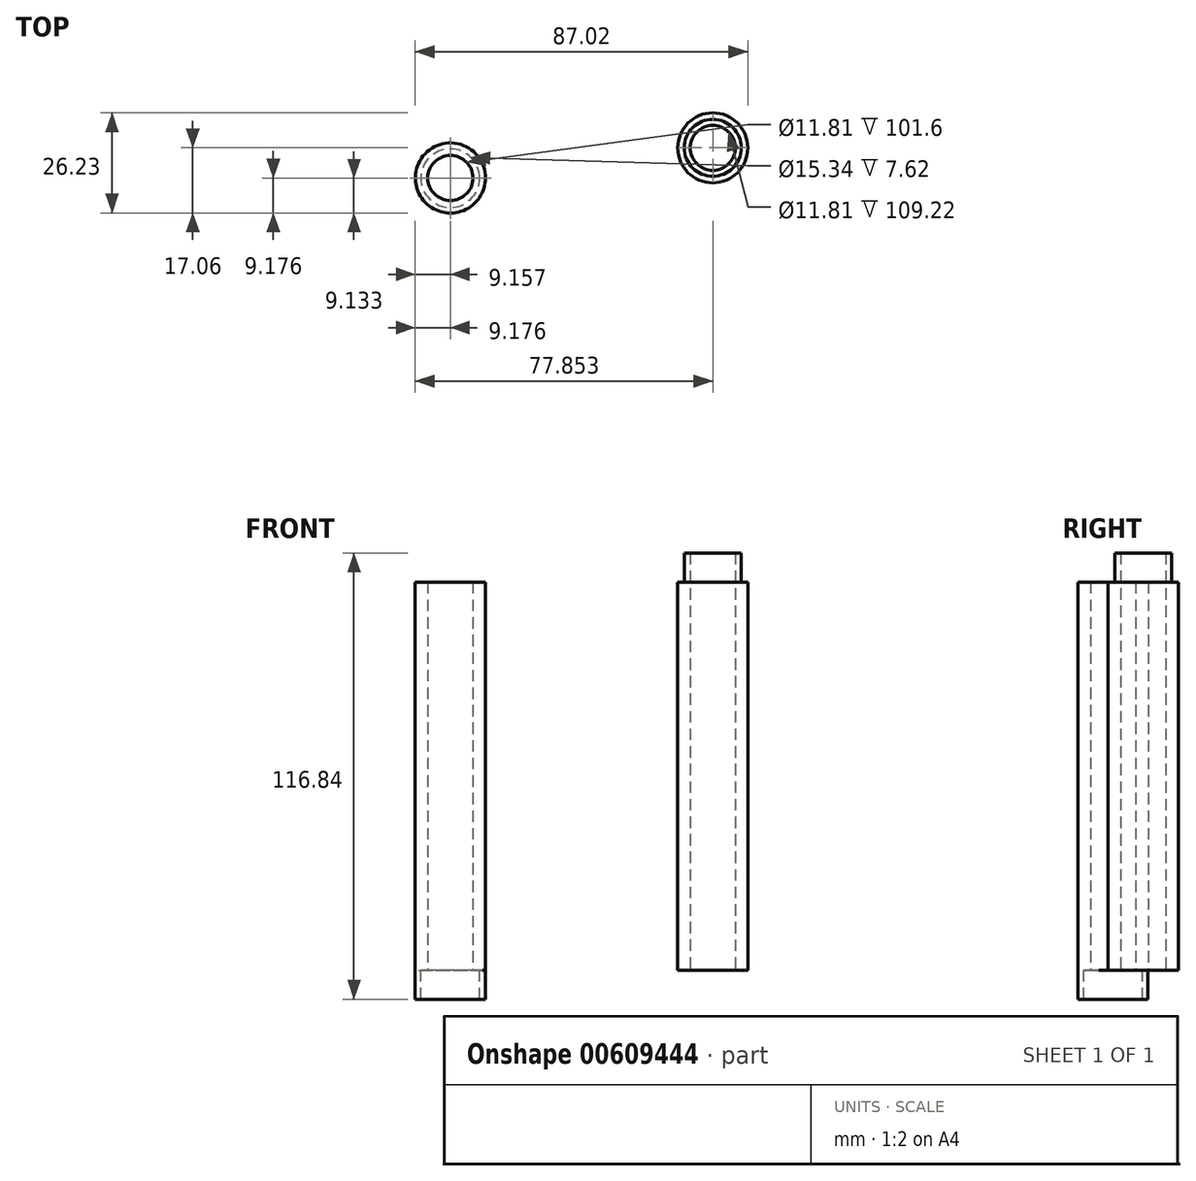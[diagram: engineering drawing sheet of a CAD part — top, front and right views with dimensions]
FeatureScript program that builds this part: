
annotation { "Feature Type Name" : "Feature", "Feature Type Description" : "" }
export const myFeature = defineFeature(function(context is Context, id is Id, definition is map)
    precondition{}
    {
        {
            var Q0;
            Q0=qCreatedBy(makeId("Top.planeOp"),FACE);
            var sketch = newSketch(context, id + "F0", { "sketchPlane" : qUnion([Q0])});
            skCircle(sketch, "E0", {"center": v(29.3, 25.7) * mm, "radius": 7.67 * mm});
            skCircle(sketch, "E1", {"center": v(29.3, 25.7) * mm, "radius": 5.9 * mm});
            skCircle(sketch, "E2", {"center": v(29.3, 25.7) * mm, "radius": 9.17 * mm});
            skSolve(sketch);
        }
        {
            var Q0;
            Q0=makeQuery(id+"F0.imprint","IMPRINT",FACE,{"disambiguationData":[TD([[makeQuery(id+"F0.imprint","IMPRINT",EDGE,{"derivedFrom":sQuery(id+"F0.wireOp",EDGE,"E0")}),1.0]])]});
            var Q1;
            Q1=makeQuery(id+"F0.imprint","IMPRINT",FACE,{"disambiguationData":[TD([[makeQuery(id+"F0.imprint","IMPRINT",EDGE,{"derivedFrom":sQuery(id+"F0.wireOp",EDGE,"E0")}),-1.0]])]});
            extrude(context, id + "F1", {"entities" : qUnion([Q0, Q1]), "depth" : 101.6 * mm, "offsetDistance" : 25.4 * mm});
        }
        {
            var Q0;
            Q0=makeQuery(id+"F1.opExtrude","CAP_FACE",FACE,{"disambiguationData":[OSD([sQuery(id+"F0.wireOp",EDGE,"E1"),sQuery(id+"F0.wireOp",EDGE,"E2")])],"isStart":false});
            var sketch = newSketch(context, id + "F2", { "sketchPlane" : qUnion([Q0])});
            skCircle(sketch, "E3", {"center": v(29.3, 25.7) * mm, "radius": 7.45 * mm});
            skSolve(sketch);
        }
        {
            var Q0;
            Q0=makeQuery(id+"F2.imprint","IMPRINT",FACE,{"disambiguationData":[TD([[makeQuery(id+"F2.imprint","IMPRINT",EDGE,{"derivedFrom":sQuery(id+"F2.wireOp",EDGE,"E3")}),1.0]])]});
            extrude(context, id + "F3", {"entities" : qUnion([Q0]), "operationType" : NewBodyOperationType.ADD, "depth" : 7.62 * mm, "offsetDistance" : 25.4 * mm});
        }
        {
            var Q0;
            Q0=qCreatedBy(makeId("Top.planeOp"),FACE);
            var sketch = newSketch(context, id + "F4", { "sketchPlane" : qUnion([Q0])});
            skCircle(sketch, "E4", {"center": v(-39.38, 17.8) * mm, "radius": 7.67 * mm});
            skCircle(sketch, "E5", {"center": v(-39.38, 17.8) * mm, "radius": 5.9 * mm});
            skCircle(sketch, "E6", {"center": v(-39.38, 17.8) * mm, "radius": 9.17 * mm});
            skSolve(sketch);
        }
        {
            var Q0;
            Q0=makeQuery(id+"F4.imprint","IMPRINT",FACE,{"disambiguationData":[TD([[makeQuery(id+"F4.imprint","IMPRINT",EDGE,{"derivedFrom":sQuery(id+"F4.wireOp",EDGE,"E4")}),-1.0]])]});
            var Q1;
            Q1=makeQuery(id+"F4.imprint","IMPRINT",FACE,{"disambiguationData":[TD([[makeQuery(id+"F4.imprint","IMPRINT",EDGE,{"derivedFrom":sQuery(id+"F4.wireOp",EDGE,"E4")}),1.0]])]});
            extrude(context, id + "F5", {"entities" : qUnion([Q0, Q1]), "depth" : 101.6 * mm, "offsetDistance" : 25.4 * mm});
        }
        {
            var Q0;
            Q0=makeQuery(id+"F5.opExtrude","CAP_FACE",FACE,{"disambiguationData":[OSD([sQuery(id+"F4.wireOp",EDGE,"E5"),sQuery(id+"F4.wireOp",EDGE,"E6")])],"isStart":true});
            var sketch = newSketch(context, id + "F6", { "sketchPlane" : qUnion([Q0])});
            skCircle(sketch, "E7", {"center": v(-39.4, -17.76) * mm, "radius": 7.67 * mm});
            skCircle(sketch, "E8", {"center": v(-39.4, -17.76) * mm, "radius": 5.9 * mm});
            skCircle(sketch, "E9", {"center": v(-39.4, -17.76) * mm, "radius": 9.17 * mm});
            skSolve(sketch);
        }
        {
            var Q0;
            Q0=makeQuery(id+"F6.imprint","IMPRINT",FACE,{"disambiguationData":[TD([[makeQuery(id+"F6.imprint","IMPRINT",EDGE,{"derivedFrom":sQuery(id+"F6.wireOp",EDGE,"E7")}),-1.0]])]});
            extrude(context, id + "F7", {"entities" : qUnion([Q0]), "operationType" : NewBodyOperationType.ADD, "depth" : 7.62 * mm, "offsetDistance" : 25.4 * mm});
        }
    });
